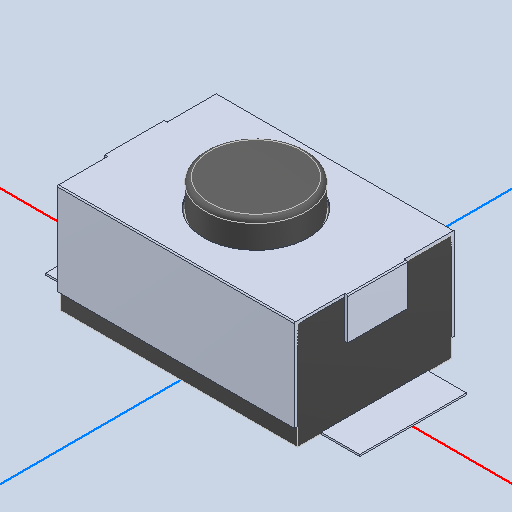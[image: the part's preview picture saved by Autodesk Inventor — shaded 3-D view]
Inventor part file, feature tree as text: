
AUTODESK INVENTOR PART (.ipt)
format: ipt  version: 2022 (Build 260153000, 153)  size: 143,872 bytes
history: native  units: mm
features: other x8, fillet x1, mirror x1
ambient origin geometry x8: Origin, YZ Plane, XZ Plane, XY Plane, X Axis, Y Axis, Z Axis, Center Point
bodies: Body1 (feature_tree), Body2 (feature_tree), Body3 (feature_tree), Body4 (feature_tree), Body5 (feature_tree)
feature tree (10):
  other  "Твердое тело1"
  other  "Твердое тело2"
  other  "Твердое тело3"
  other  "Твердое тело4"
  other  "Твердое тело5"
  other  "Boss-Extrude1"
  fillet  "Fillet3"  [1 undecoded]
  mirror  "Mirror3"
  other  "Boss-Extrude5[1]"
  other  "Boss-Extrude5[2]"
note: 1 required parameter value undecoded (feature->parameter linkage not recoverable at this tier; creation-order binding heuristic only, values carry confidence <= 0.55)
